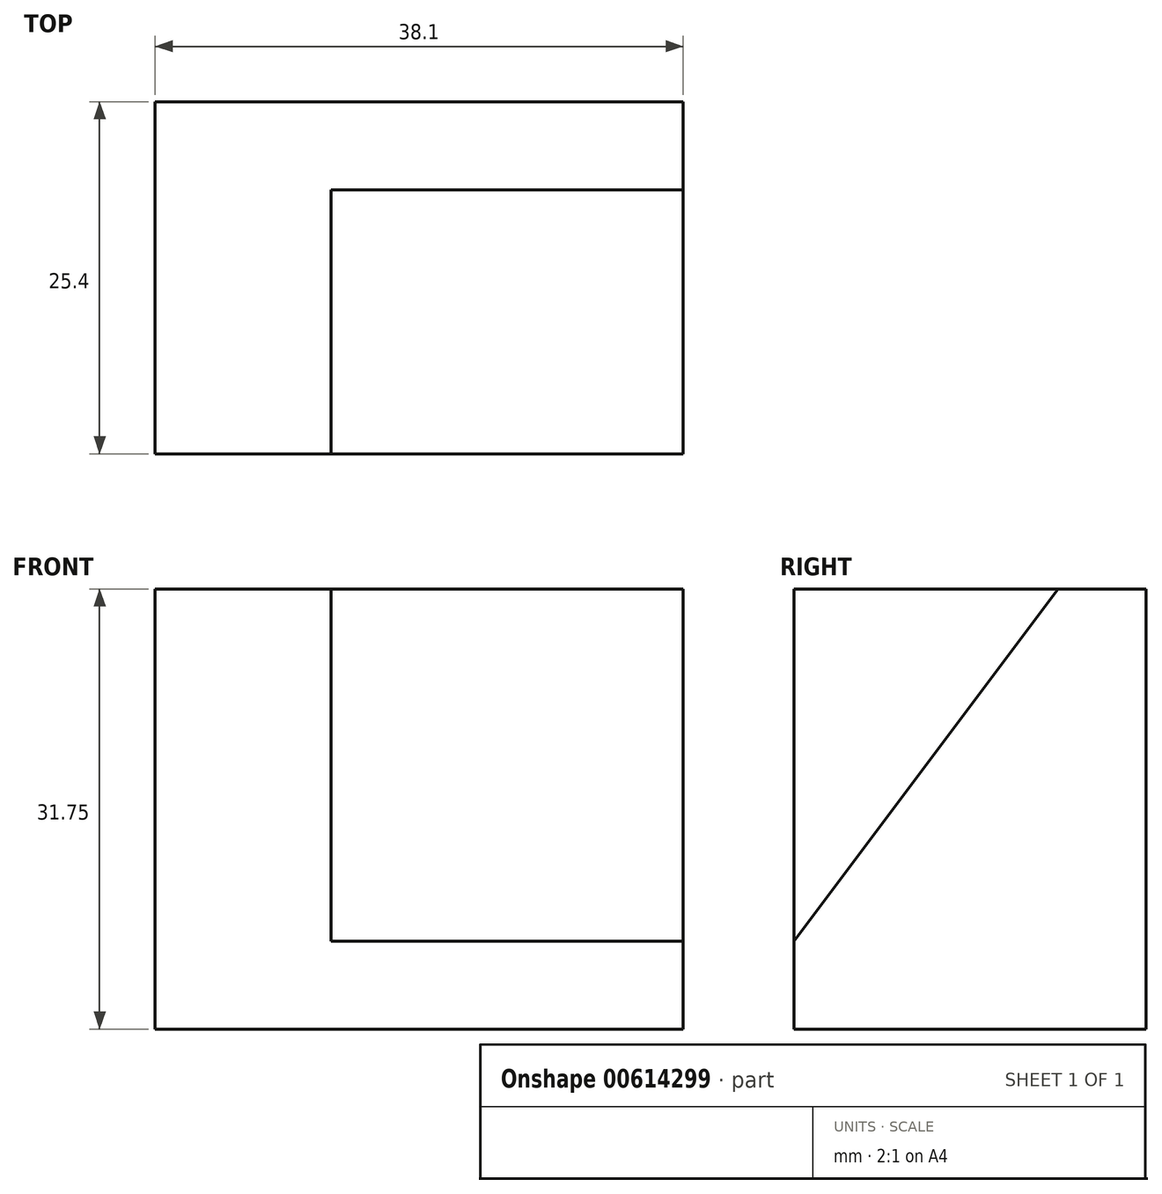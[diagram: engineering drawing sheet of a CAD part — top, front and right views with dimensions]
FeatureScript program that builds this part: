
annotation { "Feature Type Name" : "Feature", "Feature Type Description" : "" }
export const myFeature = defineFeature(function(context is Context, id is Id, definition is map)
    precondition{}
    {
        {
            var Q0;
            Q0=qCreatedBy(makeId("Front.planeOp"),FACE);
            var sketch = newSketch(context, id + "F0", { "sketchPlane" : qUnion([Q0])});
            skLineSegment(sketch, "E0", {"start": v(0, 0) * mm, "end": v(38.1, 0) * mm});
            skLineSegment(sketch, "E1", {"start": v(38.1, 0) * mm, "end": v(38.1, 31.75) * mm});
            skLineSegment(sketch, "E2", {"start": v(38.1, 31.75) * mm, "end": v(0, 31.75) * mm});
            skLineSegment(sketch, "E3", {"start": v(0, 31.75) * mm, "end": v(0, 0) * mm});
            skSolve(sketch);
        }
        {
            var Q0;
            Q0 = qSketchRegion(id + "F0", true);
            extrude(context, id + "F1", {"entities" : qUnion([Q0]), "depth" : 25.4 * mm, "offsetDistance" : 25.4 * mm});
        }
        {
            var Q0;
            Q0=makeQuery(id+"F1.opExtrude","SWEPT_FACE",FACE,{"disambiguationData":[OSD([sQuery(id+"F0.wireOp",EDGE,"E1")])]});
            var sketch = newSketch(context, id + "F2", { "sketchPlane" : qUnion([Q0])});
            skLineSegment(sketch, "E4", {"start": v(0, 31.75) * mm, "end": v(-6.35, 31.75) * mm});
            skLineSegment(sketch, "E5", {"start": v(-25.4, 0) * mm, "end": v(-25.4, 6.35) * mm});
            skLineSegment(sketch, "E6", {"start": v(-6.35, 31.75) * mm, "end": v(-25.4, 6.35) * mm});
            skLineSegment(sketch, "E7", {"start": v(-25.4, 0) * mm, "end": v(0, 0) * mm});
            skLineSegment(sketch, "E8", {"start": v(0, 0) * mm, "end": v(0, 31.75) * mm});
            skSolve(sketch);
        }
        {
            var Q0;
            {var subQ0=sQuery(id+"F2.wireOp",EDGE,"E6");Q0=makeQuery(id+"F2.imprint","IMPRINT",FACE,{"disambiguationData":[TD([[makeQuery(id+"F2.imprint","IMPRINT",EDGE,{"derivedFrom":subQ0}),-1.0]])]});}
            extrude(context, id + "F3", {"entities" : qUnion([Q0]), "operationType" : NewBodyOperationType.REMOVE, "oppositeDirection" : true, "depth" : 25.4 * mm, "offsetDistance" : 25.4 * mm});
        }
    });
